# Revit family: QUEST_DUAL_105_Dehumidifiers
name_source: partatom
category: Mechanical Equipment
revit_build: Autodesk Revit 2016 (Build: 20150714_1515(x64)
units: mm (PartAtom-declared; Revit-internal decimal feet)

## family parameters
Always vertical = Yes
Cut with Voids When Loaded = No
OmniClass Number = 23.75.00.00
OmniClass Title = Climate Control (HVAC)
Part Type = Normal
Room Calculation Point = No
Round Connector Dimension = Use Diameter
Shared = No
Work Plane-Based = No

## types (1)
- QUEST_DUAL_105_Dehumidifiers
    Blower = 257 CFM @ 0.0" WG
206 CFM @ 0.2" WG
146 CFM @ 0.4" WG
    Current Draw = 4.9 Amps
    Drain Connection = 3/4” Threaded NPT
    Drain Hose = 8’ Direct Gravity Drain Hose (5/8” ID x 7/8” OD)
    Efficiency = 8.8 Pints/KWh
    Energy Factor = 4.2 3 L/kWh
    Operating Temperature = 56°F - 95°F
    Pallet Quantity = 1 per pallet
    Power = 530 Watts
    Power Cord = 10’, 110-120 VAC, Ground
    Refrigerant = R410A, 1 lbs. 10 oz.
    Shipping Dimensions = 25”W x 29”H x 42”D
    Shipping Options = UPS and LTL
    Shipping Weight = 160 lbs.
    Supply Voltage = 110-120 VAC -1 Phase - 60 Hz.
    Trap = Yes
    URL = www.questclimate.com/product/dual-105/
    Unit Dimensions = 20.25”W x 21.75”H x 37.88”D
    Unit Weight = 140 lbs.
    Water Removal = 105 Pints/Days
    Wireframe = Yes

## geometry (parser evidence)
native form markers: Sweep x8
no freeform markers — native parametric forms only
